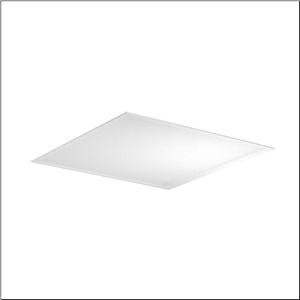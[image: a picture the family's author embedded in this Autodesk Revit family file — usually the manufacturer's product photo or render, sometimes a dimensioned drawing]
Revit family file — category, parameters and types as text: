
# Revit family: apollon_21_square_51mq12wc2454
name_source: partatom
category: Lighting Fixtures
units: mm (PartAtom-declared; Revit-internal decimal feet)

## family parameters
Cut with Voids When Loaded = No
Host = Face
Light Source = No
Part Type = Normal
Room Calculation Point = No
Round Connector Dimension = Use Diameter
Shared = No

## types (1)
- Apollon 21 square (1 x LED, 4200 lm, 24.7 W, 4000K)
    Apparent Load = 25 VA
    CIE Flux Codes = 60 87 97 100 100
    Color Rendering = 80
    Color Temperature = 4000K
    Default Elevation = 1800 mm
    Description = Apollon 21 square, office luminaire, primary optical cover: micro prismatic cover, of PMMA, CAT 2 (L<= 3000cd/m²), light emission: direct distribution, primary light characteristic: symmetric, installation type: lay-in mounting, recessed, LED, rated luminous flux: 4.200lm, luminous efficacy: 170lm/W, light colour: 840, colour temperature: 4000K, control gear: DALI 2, Multilumen, with terminal, 5-pole, mains connection: 220..240V, AC/DC, 0/50..60Hz, rated input power: 24.7W, suitable for self-contained emergency lighting element 59MQE002602A with integrated self-test function according to EN 60598-2-22, housing, of aluminium, coated, traffic white (RAL 9016), module: M600, length: 595mm, width: 595mm, height: 55mm, housing upper side, of sheet steel, galvanised, protection rating (complete): IP20, protection rating (lamp compartment, on room side): IP54, insulation class (complete): insulation class II (safety insulation), certification: CE, ENEC, UKCA, impact resistance: IK03, permissible operating ambient temperature: -20..+45°C, standard: EN 60598-2-22, corresponds to IFS (International Featured Standards) requirements for safety and quality in the food industry, packaging unit: 1 piece
    Height = 0 mm  [stored 0 ft]
    Lamp = 1 x LED
    Lamp Light Flux = 4200 lm
    Lamp Power = 24.7 W
    Lamp count = 1
    Length = 595 mm
    Luminous efficacy = 170 lm/W
    Manufacturer = Siteco
    ModVariant = No
    Model = 51MQ12WC2454
    Mounting Place = Ceiling
    Mounting Type = Recessed
    Number of Poles = 1
    OnlyDefault = Yes
    Power Factor = 1
    Product Name = Apollon 21 square
    Product group = office luminaire | ceiling recessed
    ProductGroupID = 400
    Protection Class = Protection class II
    Protection Degree = IP 20
    RLX_Detail_Level = 1
    RLX_Emergency_Light_Flux = 0 lm
    RLX_Emergency_Type = 0
    RLX_Emergency_Type_DB = No
    RlxData = <blob elided: 96993 chars, md5=369a5605>
    Socket = socket
    Standby Power = 0 W
    System Light Flux = 4200 lm
    System Power = 25 W
    Type Comments = Product without accessories
    Type Image = l_1291049.jpg
    URL = http://relux.com
    VarID = ---
    Voltage = 0 V
    Weight = 0.00 kg
    Width = 595 mm

note: [stored X ft] marks values corroborated as IEEE doubles in the binary element streams (Revit-internal decimal feet)

## geometry (parser evidence)
native form markers: Blend x4, Sweep x9
no freeform markers — native parametric forms only
